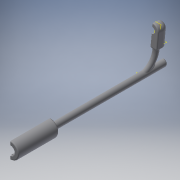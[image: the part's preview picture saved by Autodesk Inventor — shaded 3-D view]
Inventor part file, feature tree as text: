
AUTODESK INVENTOR PART (.ipt)
format: ipt  version: 2018 (Build 220112000, 112)  size: 443,904 bytes
history: native  units: mm
features: sketch x10, extrude x8, fillet x6, plane x3, projected_geometry x3, revolve x1, sweep x1
ambient origin geometry x8: Origin, YZ Plane, XZ Plane, XY Plane, X Axis, Y Axis, Z Axis, Center Point
bodies: Solid1 (feature_tree)
feature tree (32):
  revolve  "Revolution1"  [1 undecoded]
  fillet  "Fillet1"  Radius=8.0mm
  fillet  "Fillet2"  Radius=40.0mm
  fillet  "Fillet3"  [1 undecoded]
  plane  "Work Plane1"
  sweep  "Sweep1"
  extrude  "Extrusion2"  Depth=1.0mm
  fillet  "Fillet4"  Radius=1.0mm
  fillet  "Fillet5"  Radius=1.0mm
  extrude  "Extrusion3"  Depth=4.0mm
  extrude  "Extrusion4"  Depth=2.0mm
  extrude  "Extrusion5"  Depth=1.0mm
  extrude  "Extrusion6"  Depth=18.0mm
  extrude  "Extrusion7"  Depth=16.0mm
  plane  "Work Plane3"
  extrude  "Extrusion8"  Depth=12.0mm
  plane  "Work Plane5"
  extrude  "Extrusion9"  Depth=6.0mm
  fillet  "Fillet6"  Radius=6.0mm
  sketch  "Sketch6"  dims[d0=150.0mm d1=3.5mm d3=8.0mm d4=40.0mm d5=90.0deg]
  sketch  "Sketch8"  dims[d20=1.5mm d21=1.5mm]
  sketch  "Sketch9"  dims[d22=1.5mm d23=1.0mm d24=1.0mm d25=1.0mm]
  projected_geometry  "Projected Loop3"
  sketch  "Sketch10"  dims[d26=1.5mm d27=4.0mm]
  projected_geometry  "Projected Loop4"
  sketch  "Sketch11"  dims[d29=9.0mm d30=2.0mm]
  sketch  "Sketch12"  dims[d31=1.0mm d32=1.0mm]
  sketch  "Sketch13"  dims[d33=-23.0mm d38=18.0mm]
  sketch  "Sketch14"  dims[d39=18.0mm d40=16.0mm]
  sketch  "Sketch15"  dims[d41=0.0mm d42=0.0mm d43=12.0mm]
  projected_geometry  "Projected Loop5"
  sketch  "Sketch16"  dims[d44=5.0mm d45=6.0mm d46=6.0mm d47=20.0mm d48=0.0mm d49=6.0mm d50=1.0mm d51=4.0mm d52=5.5mm d53=8.0mm d54=0.0mm d55=10.0mm d56=0.0mm d57=50.0mm d58=0.0mm d59=1.4mm d60=0.0mm d62=15.0mm d63=0.0mm d64=-3.0mm d65=6.5mm d66=1.1mm d67=0.0mm d68=-3.0mm d69=10.0mm d70=0.0mm d71=0.5mm d72=6.0mm d73=8.0mm d74=8.0mm d75=0.0mm]
note: 2 required parameter values undecoded (feature->parameter linkage not recoverable at this tier; creation-order binding heuristic only, values carry confidence <= 0.55)